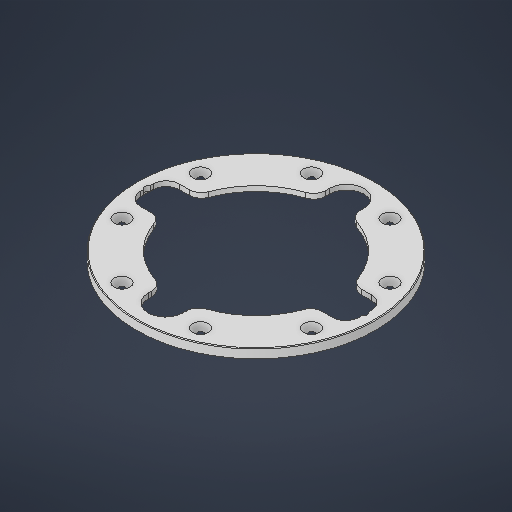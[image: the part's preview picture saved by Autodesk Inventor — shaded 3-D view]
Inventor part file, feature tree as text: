
AUTODESK INVENTOR PART (.ipt)
format: ipt  version: 2025 (Build 290162000, 162)  size: 316,928 bytes
history: native  units: in
note: dims shown in document units (in); Inventor stores cm internally (conversion verified against a paired STEP export)
features: sketch x5, extrude x3, hole x3, chamfer x1
ambient origin geometry x8: Origin, YZ Plane, XZ Plane, XY Plane, X Axis, Y Axis, Z Axis, Center Point
bodies: Solid1 (feature_tree)
feature tree (12):
  sketch  "Sketch1"  dims[d2=4.3701in d10=0.2559in d11=0.0in]
  extrude  "Extrusion1"  Depth=0.2559in TaperAngle=0.0deg
  extrude  "Extrusion2"  Depth=0.1378in
  sketch  "Sketch2"  dims[d12=0.1378in d13=0.0in d14=5.7087in]
  hole  "Hole1"  [1 undecoded]
  chamfer  "Chamfer2"  Distance=0.3937in
  hole  "Hole2"  [1 undecoded]
  extrude  "Extrusion4"  Depth=0.3937in
  hole  "Hole4"  [1 undecoded]
  sketch  "Sketch4"  dims[d27=0.1378in d28=0.2362in d29=0.1575in d30=0.0787in d31=90.0deg d32=0.3465in d33=0.0in d34=0.0197in d35=0.0787in d36=45.0deg]
  sketch  "Sketch Circular Pattern3"  dims[d15=0.0787in]
  sketch  "Sketch5"  dims[d37=0.1628in d38=0.3937in d39=0.4409in d40=0.0787in d41=90.0deg d42=0.5591in d43=0.0in d60=4.4094in d74=0.3937in d75=0.0in d76=4.3307in d77=90.0deg d78=0.315in d79=0.9843in d80=2.9921in d81=0.3937in d82=2.5236in d83=0.3937in d84=0.4291in d85=0.0492in d86=0.315in d87=22.5deg d88=0.1969in d89=3.1496in d91=360.0deg d93=0.1969in d94=0.1969in d95=0.2165in d96=0.3937in d97=0.4409in d98=0.0787in d99=90.0deg d100=0.5591in d101=0.0in d102=5.9843in]
note: 3 required parameter values undecoded (feature->parameter linkage not recoverable at this tier; creation-order binding heuristic only, values carry confidence <= 0.55)
